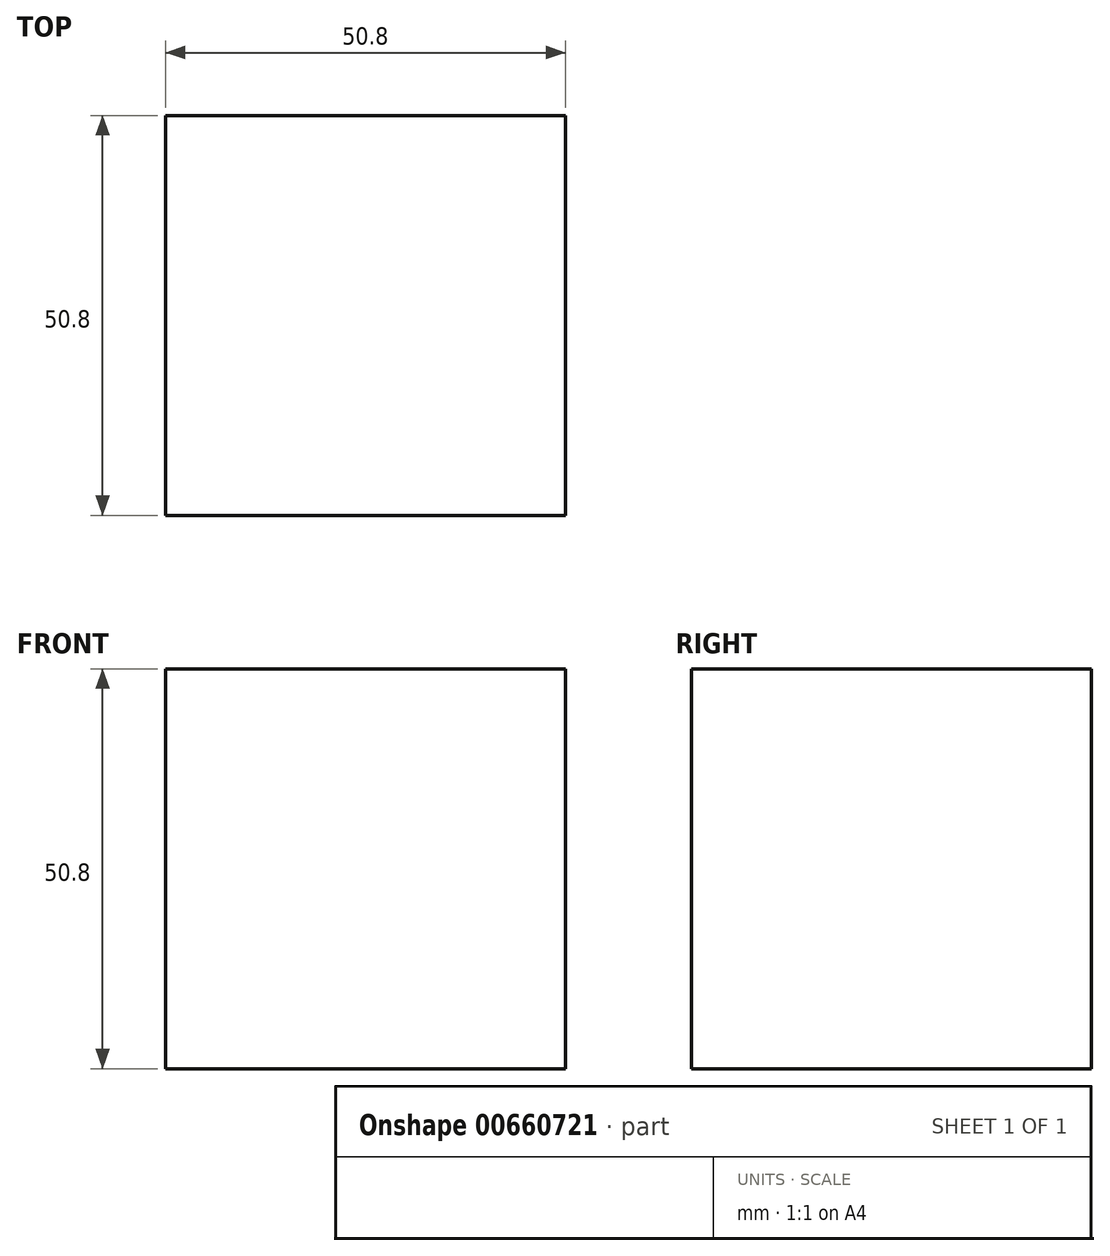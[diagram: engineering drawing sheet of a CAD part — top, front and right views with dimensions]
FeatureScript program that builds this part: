
annotation { "Feature Type Name" : "Feature", "Feature Type Description" : "" }
export const myFeature = defineFeature(function(context is Context, id is Id, definition is map)
    precondition{}
    {
        {
            var Q0;
            Q0=qCreatedBy(makeId("Front.planeOp"),FACE);
            var sketch = newSketch(context, id + "F0", { "sketchPlane" : qUnion([Q0])});
            skLineSegment(sketch, "E0.bottom", {"start": v(-24.26, 15.84) * mm, "end": v(26.54, 15.84) * mm});
            skLineSegment(sketch, "E0.top", {"start": v(-24.26, -34.96) * mm, "end": v(26.54, -34.96) * mm});
            skLineSegment(sketch, "E0.left", {"start": v(-24.26, 15.84) * mm, "end": v(-24.26, -34.96) * mm});
            skLineSegment(sketch, "E0.right", {"start": v(26.54, 15.84) * mm, "end": v(26.54, -34.96) * mm});
            skSolve(sketch);
        }
        {
            var Q0;
            Q0=makeQuery(id+"F0.imprint","IMPRINT",FACE,{"disambiguationData":[TD([[makeQuery(id+"F0.imprint","IMPRINT",EDGE,{"derivedFrom":sQuery(id+"F0.wireOp",EDGE,"E0.bottom")}),-1.0]])]});
            extrude(context, id + "F1", {"entities" : qUnion([Q0]), "depth" : 50.8 * mm, "offsetDistance" : 25.4 * mm});
        }
    });
